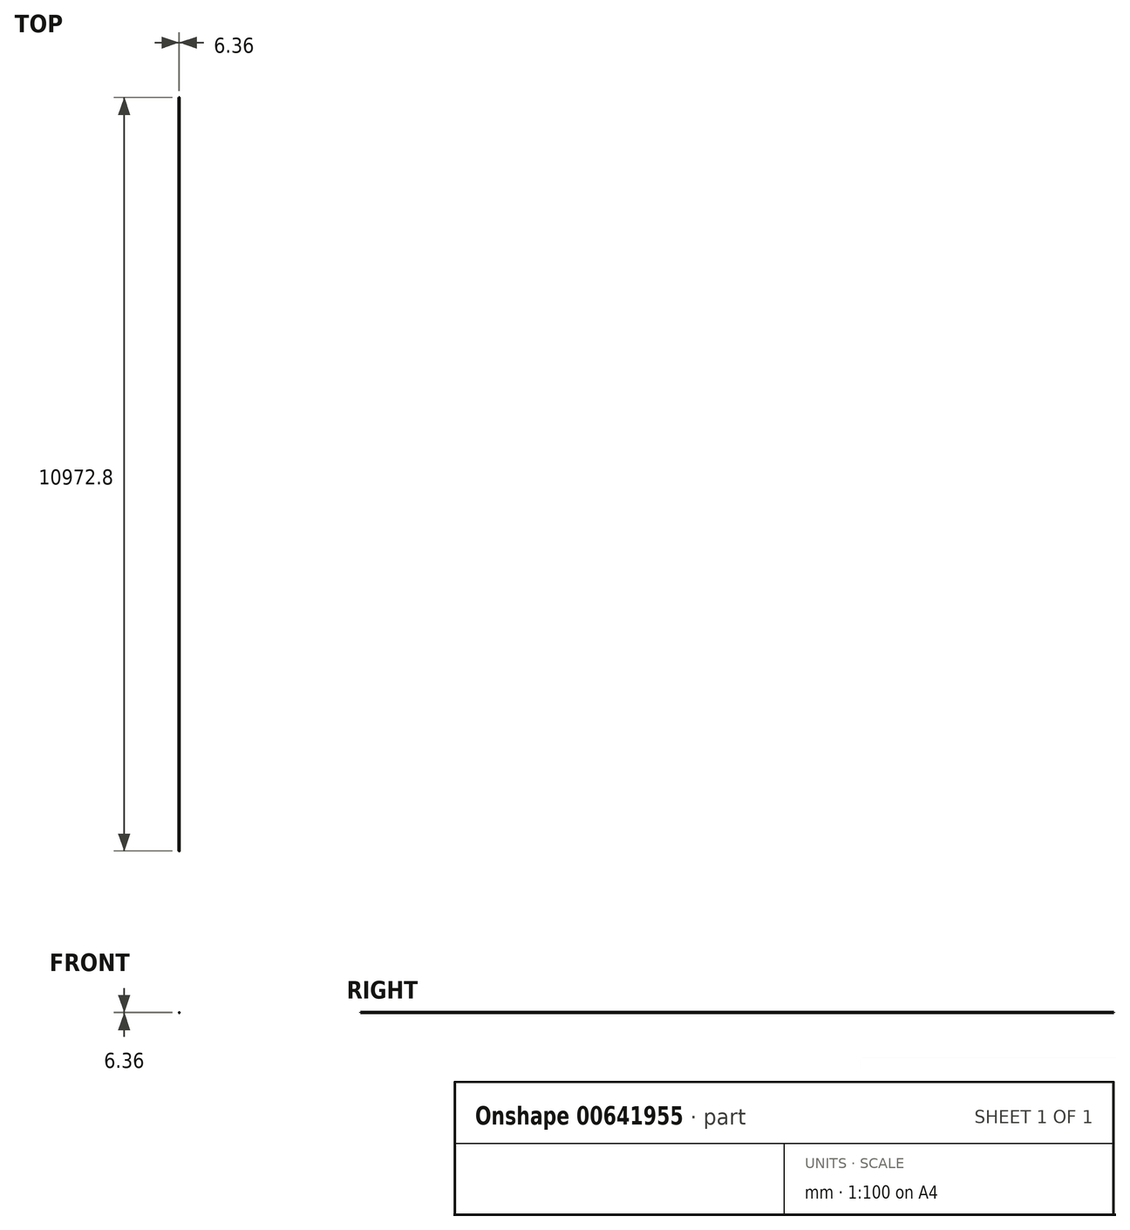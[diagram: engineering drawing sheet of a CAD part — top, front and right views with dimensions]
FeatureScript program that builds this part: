
annotation { "Feature Type Name" : "Feature", "Feature Type Description" : "" }
export const myFeature = defineFeature(function(context is Context, id is Id, definition is map)
    precondition{}
    {
        {
            var Q0;
            Q0=qCreatedBy(makeId("Front.planeOp"),FACE);
            var sketch = newSketch(context, id + "F0", { "sketchPlane" : qUnion([Q0])});
            skCircle(sketch, "E0", {"center": v(0, 0) * mm, "radius": 3.18 * mm});
            skSolve(sketch);
        }
        {
            var Q0;
            Q0 = qSketchRegion(id + "F0", true);
            extrude(context, id + "F1", {"entities" : qUnion([Q0]), "depth" : 10972.8 * mm, "offsetDistance" : 30.48 * mm});
        }
    });
